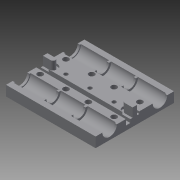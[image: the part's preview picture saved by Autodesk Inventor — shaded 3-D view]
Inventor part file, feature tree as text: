
AUTODESK INVENTOR PART (.ipt)
format: ipt  version: 2014 SP1 (Build 180222100, 222)  size: 321,536 bytes
history: native  units: mm
features: sketch x18, extrude x17, plane x2, hole x1
ambient origin geometry x8: Origin, YZ Plane, XZ Plane, XY Plane, X Axis, Y Axis, Z Axis, Center Point
bodies: Body1 (feature_tree)
feature tree (38):
  extrude  "Extrusion4"  Depth=70.0mm
  extrude  "Extrusion5"  Depth=21.0mm
  extrude  "Extrusion6"  Depth=10.0mm
  extrude  "Extrusion7"  Depth=11.5mm
  extrude  "Extrusion8"  Depth=23.0mm
  extrude  "Extrusion9"  Depth=11.5mm
  extrude  "Extrusion10"  Depth=5.0mm
  plane  "Work Plane1"
  extrude  "Extrusion11"  Depth=5.0mm
  plane  "Work Plane4"
  extrude  "Extrusion13"  Depth=5.0mm
  extrude  "Extrusion14"  Depth=5.0mm
  extrude  "Extrusion15"  Depth=22.5mm
  extrude  "Extrusion16"  Depth=15.0mm
  hole  "Hole2"  [1 undecoded]
  sketch  "Sketch25"  dims[d63=10.0mm d64=0.0mm d72=2.0mm d73=0.0mm]
  extrude  "Extrusion23"  Depth=2.0mm TaperAngle=0.0deg
  extrude  "Extrusion24"  Depth=2.0mm TaperAngle=0.0deg
  extrude  "Extrusion25"  Depth=2.0mm TaperAngle=0.0deg
  extrude  "Extrusion26"  Depth=2.0mm TaperAngle=0.0deg
  extrude  "Extrusion27"  Depth=11.0mm
  sketch  "Sketch1"  dims[d0=80.0mm d1=70.0mm]
  sketch  "Sketch4"  dims[d2=21.0mm d3=21.0mm]
  sketch  "Sketch5"  dims[d39=10.0mm d40=10.0mm]
  sketch  "Sketch7"  dims[d41=23.0mm d42=11.5mm]
  sketch  "Sketch8"  dims[d43=66.0mm d44=23.0mm]
  sketch  "Sketch9"  dims[d45=66.0mm d46=11.5mm]
  sketch  "Sketch10"  dims[d47=5.0mm d48=5.0mm]
  sketch  "Sketch11"  dims[d49=5.0mm d50=5.0mm]
  sketch  "Sketch14"  dims[d51=5.0mm d52=5.0mm]
  sketch  "Sketch15"  dims[d53=5.0mm d54=5.0mm]
  sketch  "Sketch16"  dims[d55=14.0mm d56=0.0mm d57=22.5mm]
  sketch  "Sketch17"  dims[d58=45.0mm d59=15.0mm]
  sketch  "Sketch18"  dims[d60=10.0mm d61=0.0mm d62=15.0mm]
  sketch  "Sketch26"  dims[d74=13.0mm d75=2.0mm d76=0.0mm]
  sketch  "Sketch27"  dims[d77=13.0mm d78=2.0mm d79=0.0mm]
  sketch  "Sketch28"  dims[d80=13.0mm d81=2.0mm d82=0.0mm]
  sketch  "Sketch29"  dims[d83=-29.0mm d84=11.0mm d85=2.0mm d86=2.0mm d87=0.0mm d93=-27.0mm d97=2.0mm d98=0.0mm d99=11.0mm d100=15.0mm d101=2.0mm d102=0.0mm d103=11.0mm d104=15.0mm d105=2.0mm d106=0.0mm d107=10.0mm d108=0.0mm d109=3.5mm d110=6.0mm d111=6.0mm d112=4.0mm d113=90.0deg d114=8.0mm d115=20.594885mm d137=2.0mm d138=0.0mm d141=2.0mm d142=0.0mm d143=6.0mm d144=0.0mm d145=6.0mm d146=0.0mm d147=5.0mm d148=0.0mm]
note: 1 required parameter value undecoded (feature->parameter linkage not recoverable at this tier; creation-order binding heuristic only, values carry confidence <= 0.55)
